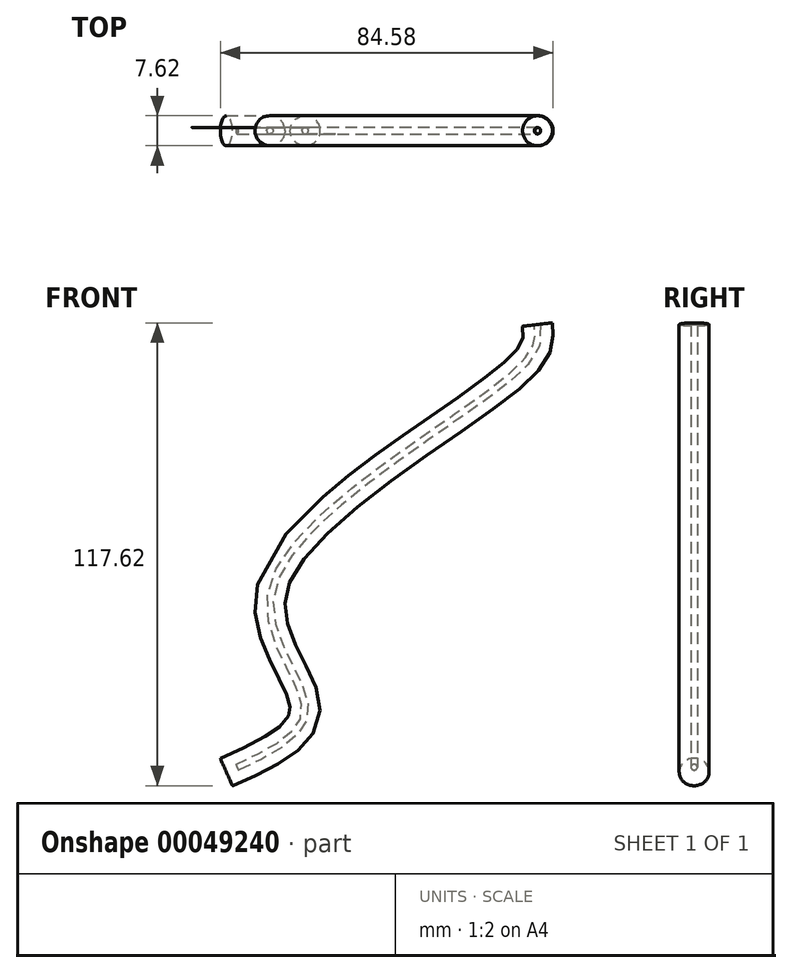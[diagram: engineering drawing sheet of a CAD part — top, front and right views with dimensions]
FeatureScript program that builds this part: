
annotation { "Feature Type Name" : "Feature", "Feature Type Description" : "" }
export const myFeature = defineFeature(function(context is Context, id is Id, definition is map)
    precondition{}
    {
        {
            var Q0;
            Q0=qCreatedBy(makeId("Front.planeOp"),FACE);
            var sketch = newSketch(context, id + "F0", { "sketchPlane" : qUnion([Q0])});
            skFitSpline(sketch, "E0", {"points": [v(19.34, 0) * mm, v(39.38, 15.68) * mm, v(31.06, 47.21) * mm, v(95, 103.65) * mm, v(98.38, 113.7) * mm], "startDerivative": vector(136.89, 60.45) * mm, "endDerivative": vector(-7.14, 61.36) * mm});
            skSolve(sketch);
        }
        {
            var Q0;
            Q0=sQuery(id+"F0.wireOp",VERTEX,"E0.start");
            var Q1;
            Q1=sQuery(id+"F0.wireOp",EDGE,"E0");
            cPlane(context, id + "F1", {"entities" : qUnion([Q0, Q1]), "cplaneType" : CPlaneType.CURVE_POINT, "offset" : 152.4 * mm, "width" : 152.4 * mm, "height" : 152.4 * mm});
        }
        {
            var Q0;
            Q0=qCreatedBy(id+"F1.planeOp",FACE);
            var sketch = newSketch(context, id + "F2", { "sketchPlane" : qUnion([Q0])});
            skCircle(sketch, "E1", {"center": v(0, -7.81) * mm, "radius": 3.81 * mm});
            skSolve(sketch);
        }
        {
            var Q0;
            Q0 = qSketchRegion(id + "F2", true);
            var Q1;
            Q1 = qConstructionFilter(qBodyType(qCreatedBy(id + "F0" ,EDGE), BodyType.WIRE), ConstructionObject.NO);
            sweep(context, id + "F3", {"profiles" : qUnion([Q0]), "path" : qUnion([Q1])});
        }
        {
            var Q0;
            Q0=makeQuery(id+"F3.opSweep","CAP_FACE",FACE,{"disambiguationData":[OSD([sQuery(id+"F0.wireOp",VERTEX,"E0.end"),sQuery(id+"F2.wireOp",EDGE,"E1")])],"isStart":false});
            shell(context, id + "F4", {"entities" : qUnion([Q0]), "thickness" : 3 * mm});
        }
    });
